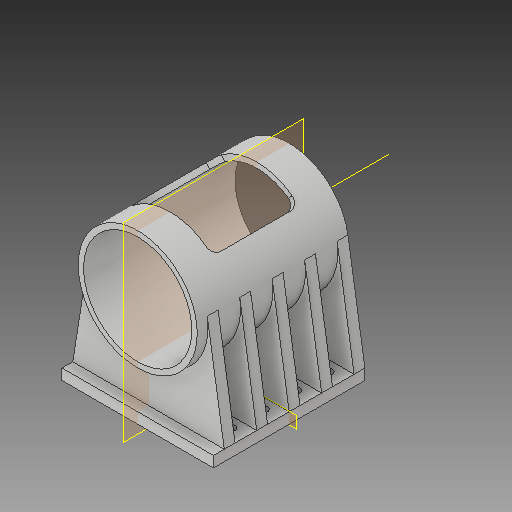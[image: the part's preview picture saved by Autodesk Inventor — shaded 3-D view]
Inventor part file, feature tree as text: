
AUTODESK INVENTOR PART (.ipt)
format: ipt  version: 2017 (Build 210142000, 142)  size: 253,952 bytes
history: native  units: mm
features: sketch x4, projected_geometry x4, extrude x3, plane x2, pattern_linear x2, other x1, revolve x1, fillet x1, hole x1, mirror x1
ambient origin geometry x8: Origin, YZ Plane, XZ Plane, XY Plane, X Axis, Y Axis, Z Axis, Center Point
bodies: Solid1 (feature_tree)
feature tree (20):
  extrude  "Extrusion1"  Depth=70.0mm
  plane  "Work Plane2"
  sketch  "Sketch2"  dims[d2=5.0mm d3=0.0mm d4=50.0mm]
  extrude  "Extrusion2"  Depth=5.0mm
  pattern_linear  "Rectangular Pattern1"  Count1=5 Spacing1=15.0mm
  extrude  "Extrusion3"  Depth=15.0mm TaperAngle=0.0deg
  plane  "Work Plane1"
  sketch  "Sketch3"  dims[d6=55.0mm]
  other  "Work Axis1"
  revolve  "Revolution1"  Angle=90.0deg
  fillet  "Fillet1"  Radius=15.0mm
  hole  "Hole1"  [1 undecoded]
  pattern_linear  "Rectangular Pattern2"  Spacing1=4.0mm  [1 undecoded]
  mirror  "Mirror1"
  sketch  "Sketch1"  dims[d0=70.0mm d1=70.0mm]
  sketch  "Sketch4"  dims[d7=5.0mm d8=0.0mm d9=50.0mm d11=15.0mm d12=70.0mm d13=73.0mm d14=0.0mm d15=0.0mm d18=90.0deg d19=15.0mm d20=15.0mm d21=4.0mm d22=50.0mm d23=7.0mm d24=7.0mm d25=4.0mm d26=6.35mm d27=4.0mm d28=2.0mm d29=90.0deg d30=9.525mm d31=0.0mm d32=40.0mm d34=15.0mm]
  projected_geometry  "Projected Loop1"
  projected_geometry  "Projected Loop2"
  projected_geometry  "Projected Loop3"
  projected_geometry  "Projected Loop4"
note: 2 required parameter values undecoded (feature->parameter linkage not recoverable at this tier; creation-order binding heuristic only, values carry confidence <= 0.55)
